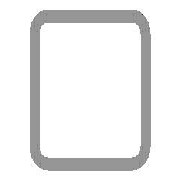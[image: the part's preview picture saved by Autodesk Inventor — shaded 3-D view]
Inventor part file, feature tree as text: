
AUTODESK INVENTOR PART (.ipt)
format: ipt  version: 2025 (Build 290162010, 162A)  size: 130,560 bytes
history: native  units: mm (DEFAULTED — no unit token found)
features: other x4, sketch x1, plane x1
ambient origin geometry x8: Origin, YZ Plane, XZ Plane, XY Plane, X Axis, Y Axis, Z Axis, Center Point
bodies: Solid1 (feature_tree), Body (feature_tree)
feature tree (6):
  parser-record x1  (decoder bookkeeping rows leaked as tree rows — omitted from the tree; the rows remain in map.json)
  other  "Driven Length"
  other  "Start Plane"
  other  "End Plane"
  sketch  "Sketch3"  dims[d3=3745.0mm d4=0.0mm d7=4.0mm d9=40.0mm d11=40.0mm d12=2.0mm d13=-0.0mm d14=3745.0mm d15=20.0mm d16=20.0mm d17=90.0deg d18=3745.0mm]
  plane  "Work Plane3"
